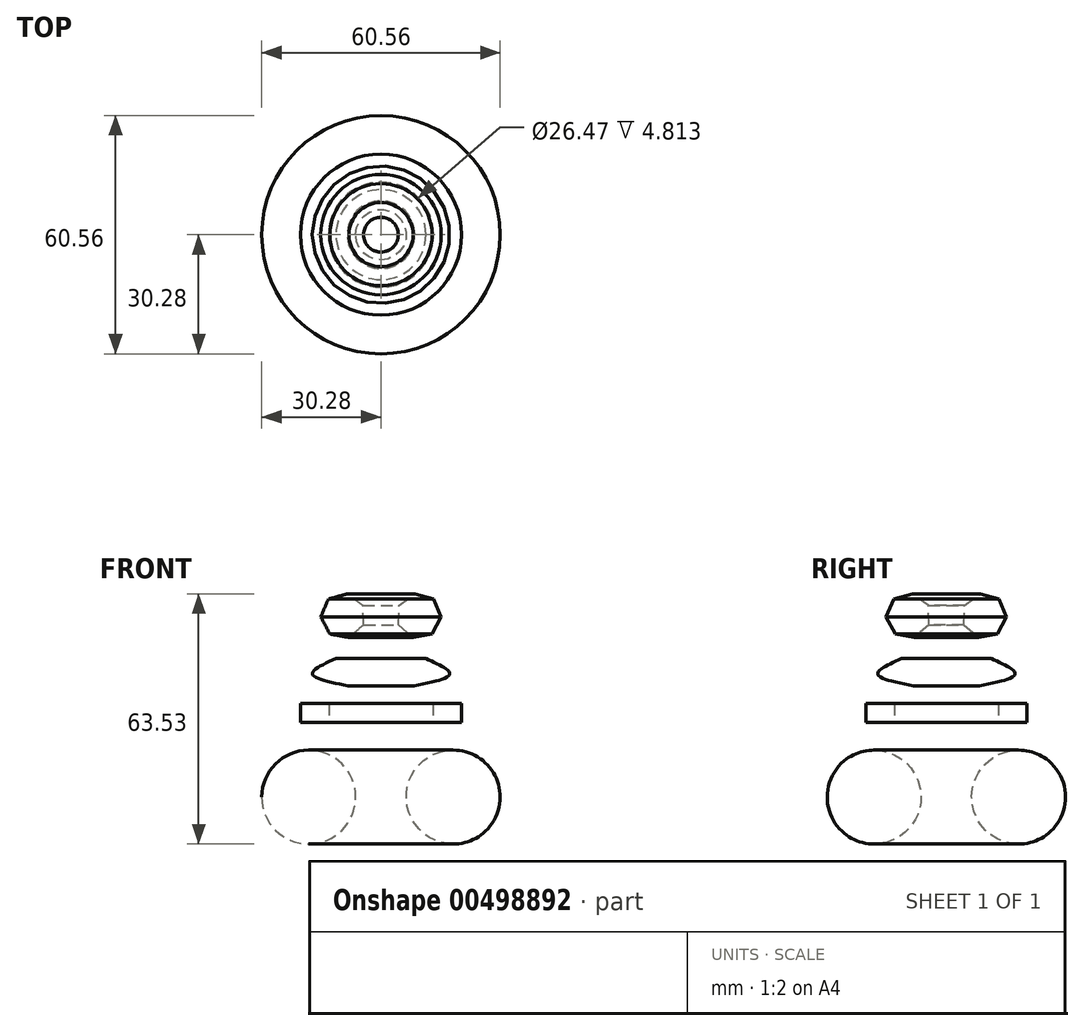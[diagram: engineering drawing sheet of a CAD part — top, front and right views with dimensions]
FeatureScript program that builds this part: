
annotation { "Feature Type Name" : "Feature", "Feature Type Description" : "" }
export const myFeature = defineFeature(function(context is Context, id is Id, definition is map)
    precondition{}
    {
        {
            var Q0;
            Q0=qCreatedBy(makeId("Front.planeOp"),FACE);
            var sketch = newSketch(context, id + "F0", { "sketchPlane" : qUnion([Q0])});
            skLineSegment(sketch, "E0", {"start": v(0, 73.1) * mm, "end": v(0, 0) * mm, "construction": true});
            skCircle(sketch, "E1", {"center": v(18.35, 21.06) * mm, "radius": 11.93 * mm});
            skLineSegment(sketch, "E2.bottom", {"start": v(13.23, 44.82) * mm, "end": v(20.45, 44.82) * mm});
            skLineSegment(sketch, "E2.top", {"start": v(13.23, 40) * mm, "end": v(20.45, 40) * mm});
            skLineSegment(sketch, "E2.left", {"start": v(13.23, 44.82) * mm, "end": v(13.23, 40) * mm});
            skLineSegment(sketch, "E2.right", {"start": v(20.45, 44.82) * mm, "end": v(20.45, 40) * mm});
            skCircle(sketch, "E3.cCircle", {"center": v(9.63, 67.08) * mm, "radius": 5.11 * mm, "construction": true});
            skLineSegment(sketch, "E3.0", {"start": v(15.3, 66.84) * mm, "end": v(12.98, 62.5) * mm});
            skLineSegment(sketch, "E3.1", {"start": v(12.98, 62.5) * mm, "end": v(8.14, 61.6) * mm});
            skLineSegment(sketch, "E3.2", {"start": v(8.14, 61.6) * mm, "end": v(4.41, 64.83) * mm});
            skLineSegment(sketch, "E3.3", {"start": v(4.41, 64.83) * mm, "end": v(4.62, 69.75) * mm});
            skLineSegment(sketch, "E3.4", {"start": v(4.62, 69.75) * mm, "end": v(8.6, 72.66) * mm});
            skLineSegment(sketch, "E3.5", {"start": v(8.6, 72.66) * mm, "end": v(13.34, 71.36) * mm});
            skLineSegment(sketch, "E3.6", {"start": v(13.34, 71.36) * mm, "end": v(15.3, 66.84) * mm});
            skPoint(sketch, "E3.0.midPoint", {"position": v(14.14, 64.67) * mm});
            skFitSpline(sketch, "E4", {"points": [v(11.43, 56.25) * mm, v(17.45, 52.34) * mm, v(8.42, 49.33) * mm], "startDerivative": vector(19.87, -9.06) * mm, "endDerivative": vector(-24.84, -4.87) * mm});
            skSolve(sketch);
        }
        {
            var Q0;
            Q0 = qConstructionFilter(qBodyType(qCreatedBy(id + "F0" ,EDGE), BodyType.WIRE), ConstructionObject.NO);
            var Q1;
            Q1=sQuery(id+"F0.wireOp",EDGE,"E0");
            revolve(context, id + "F1", {"bodyType" : ToolBodyType.SURFACE, "surfaceEntities" : qUnion([Q0]), "axis" : qUnion([Q1]), "revolveType" : RevolveType.FULL});
        }
    });
